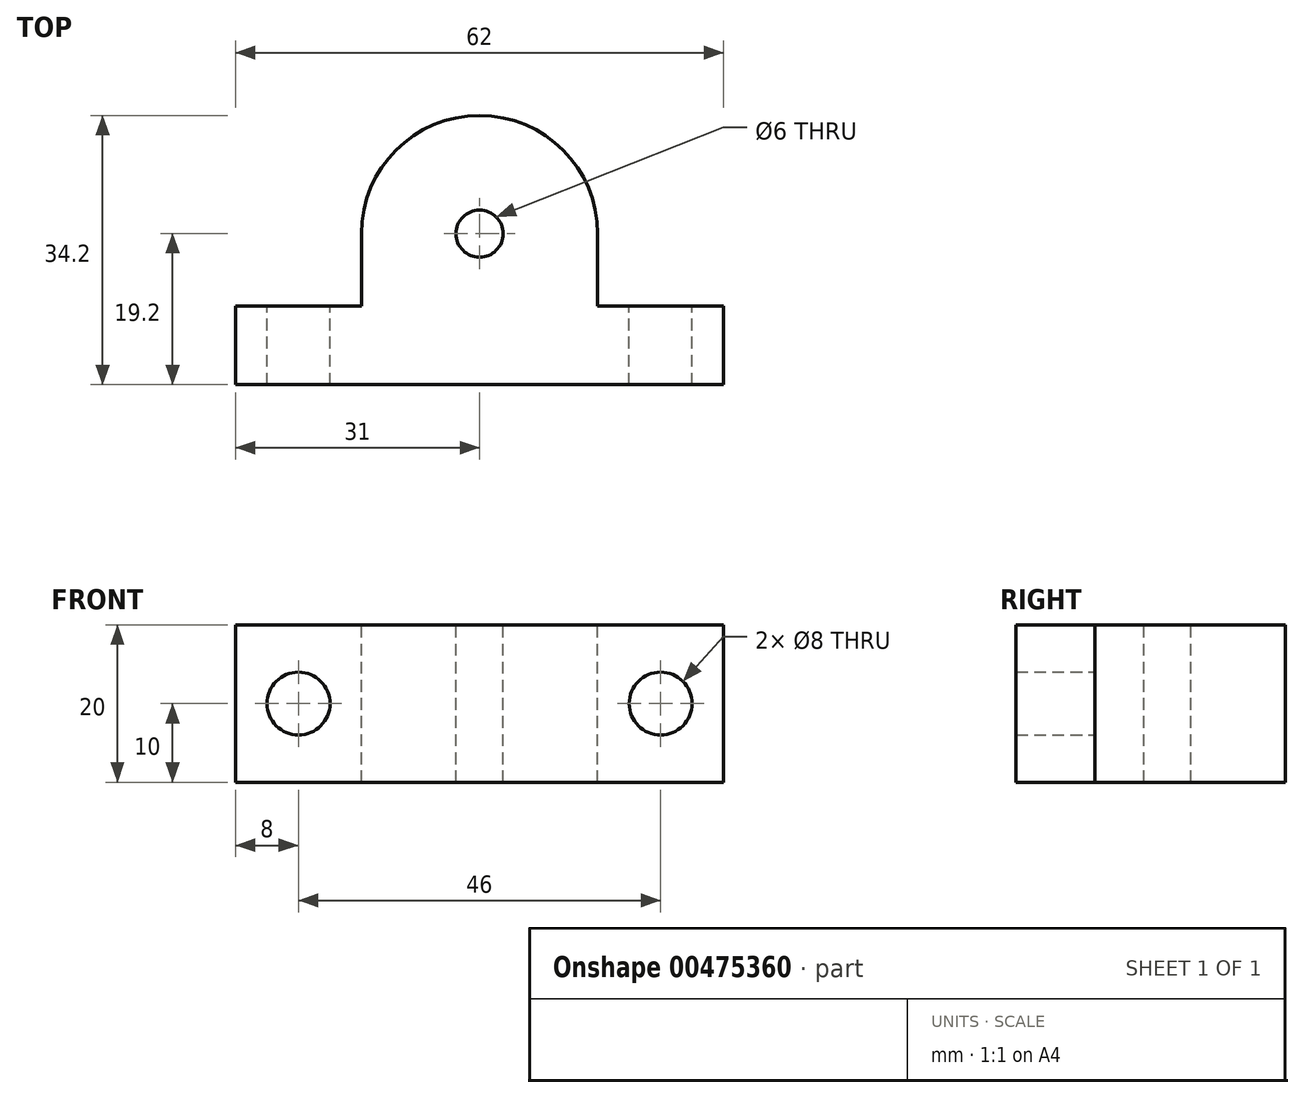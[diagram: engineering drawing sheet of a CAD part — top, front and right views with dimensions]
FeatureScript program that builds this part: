
annotation { "Feature Type Name" : "Feature", "Feature Type Description" : "" }
export const myFeature = defineFeature(function(context is Context, id is Id, definition is map)
    precondition{}
    {
        {
            var Q0;
            Q0=qCreatedBy(makeId("Top.planeOp"),FACE);
            var sketch = newSketch(context, id + "F0", { "sketchPlane" : qUnion([Q0])});
            skLineSegment(sketch, "E0.bottom", {"start": v(28, -19.2) * mm, "end": v(-28, -19.2) * mm});
            skLineSegment(sketch, "E0.top", {"start": v(28, 0) * mm, "end": v(-28, 0) * mm});
            skLineSegment(sketch, "E0.left", {"start": v(28, -19.2) * mm, "end": v(28, 0) * mm});
            skLineSegment(sketch, "E0.right", {"start": v(-28, -19.2) * mm, "end": v(-28, 0) * mm});
            skPoint(sketch, "E0.middle", {"position": v(0, -9.6) * mm});
            skCircle(sketch, "E1", {"center": v(0, 0) * mm, "radius": 9.5 * mm});
            skArc(sketch, "E2", {"start": v(-15, 0) * mm, "mid": v(0, 15) * mm, "end": v(15, 0) * mm});
            skLineSegment(sketch, "E3", {"start": v(-28, -9.2) * mm, "end": v(-11, -9.2) * mm});
            skLineSegment(sketch, "E4", {"start": v(-11, -9.2) * mm, "end": v(-11, -19.2) * mm});
            skLineSegment(sketch, "E5", {"start": v(11, -19.2) * mm, "end": v(11, -9.2) * mm});
            skLineSegment(sketch, "E6", {"start": v(11, -9.2) * mm, "end": v(28, -9.2) * mm});
            skLineSegment(sketch, "E7", {"start": v(-28, 0) * mm, "end": v(-28, 8.5) * mm});
            skLineSegment(sketch, "E8", {"start": v(-28, 8.5) * mm, "end": v(28, 8.5) * mm});
            skLineSegment(sketch, "E9", {"start": v(28, 8.5) * mm, "end": v(28, 0) * mm});
            skPoint(sketch, "E10", {"position": v(-19, 0) * mm});
            skLineSegment(sketch, "E11", {"start": v(-28, 3.17) * mm, "end": v(-28, 0) * mm});
            skPoint(sketch, "E12", {"position": v(28, 0) * mm});
            skPoint(sketch, "E13", {"position": v(19, 0) * mm});
            skPoint(sketch, "E14", {"position": v(25.5, 0) * mm});
            skPoint(sketch, "E15", {"position": v(12.4, 0) * mm});
            skPoint(sketch, "E16", {"position": v(0, 21) * mm});
            skLineSegment(sketch, "E17", {"start": v(0, 21) * mm, "end": v(-28, 13.5) * mm});
            skPoint(sketch, "E18", {"position": v(-25.5, 0) * mm});
            skLineSegment(sketch, "E19", {"start": v(-25.5, 0) * mm, "end": v(-25.5, 14.17) * mm});
            skPoint(sketch, "E20", {"position": v(-25.5, 8.67) * mm});
            skPoint(sketch, "E21", {"position": v(-12.4, 0) * mm});
            skLineSegment(sketch, "E22", {"start": v(-25.5, 8.67) * mm, "end": v(-12.24, 8.67) * mm});
            skPoint(sketch, "E23", {"position": v(-19, 8.67) * mm});
            skLineSegment(sketch, "E24", {"start": v(31, 8.5) * mm, "end": v(31, -9.2) * mm});
            skLineSegment(sketch, "E25", {"start": v(28, 8.5) * mm, "end": v(31, 8.5) * mm});
            skLineSegment(sketch, "E26", {"start": v(-28, 8.5) * mm, "end": v(-31, 8.5) * mm});
            skLineSegment(sketch, "E27", {"start": v(-31, 8.5) * mm, "end": v(-31, -9.2) * mm});
            skLineSegment(sketch, "E28", {"start": v(-31, -9.2) * mm, "end": v(-28, -9.2) * mm});
            skLineSegment(sketch, "E29", {"start": v(31, -9.2) * mm, "end": v(28, -9.2) * mm});
            skLineSegment(sketch, "E30", {"start": v(31, -9.2) * mm, "end": v(31, -19.2) * mm});
            skLineSegment(sketch, "E31", {"start": v(31, -19.2) * mm, "end": v(28, -19.2) * mm});
            skLineSegment(sketch, "E32", {"start": v(-31, -9.2) * mm, "end": v(-31, -19.2) * mm});
            skLineSegment(sketch, "E33", {"start": v(-31, -19.2) * mm, "end": v(-28, -19.2) * mm});
            skLineSegment(sketch, "E34", {"start": v(15, 0) * mm, "end": v(15, -9.2) * mm});
            skLineSegment(sketch, "E35", {"start": v(-15, 0) * mm, "end": v(-15, -9.2) * mm});
            skSolve(sketch);
        }
        {
            var Q0;
            {var subQ1=sQuery(id+"F0.wireOp",EDGE,"E0.top");var subQ3=sQuery(id+"F0.wireOp",EDGE,"E1");var subQ4=makeQuery(id+"F0.imprint","INTERSECT",VERTEX,{"disambiguationData":[OD(1.0)],"derivedFrom":[subQ1,subQ3]});Q0=makeQuery(id+"F0.imprint","IMPRINT",FACE,{"disambiguationData":[TD([[makeQuery(id+"F0.imprint","IMPRINT",EDGE,{"disambiguationData":[TD([[subQ4,1.0]])],"derivedFrom":subQ3}),-1.0]])]});}
            var Q1;
            {var subQ0=sQuery(id+"F0.wireOp",EDGE,"E8");var subQ1=sQuery(id+"F0.wireOp",EDGE,"E1");var subQ7=makeQuery(id+"F0.imprint","INTERSECT",VERTEX,{"disambiguationData":[OD(0.0)],"derivedFrom":[subQ1,subQ0]});Q1=makeQuery(id+"F0.imprint","IMPRINT",FACE,{"disambiguationData":[TD([[makeQuery(id+"F0.imprint","IMPRINT",EDGE,{"disambiguationData":[TD([[subQ7,-1.0]])],"derivedFrom":subQ1}),-1.0]])]});}
            var Q2;
            {var subQ0=sQuery(id+"F0.wireOp",EDGE,"E1");var subQ1=sQuery(id+"F0.wireOp",EDGE,"E0.top");var subQ2=makeQuery(id+"F0.imprint","INTERSECT",VERTEX,{"disambiguationData":[OD(0.0)],"derivedFrom":[subQ1,subQ0]});Q2=makeQuery(id+"F0.imprint","IMPRINT",FACE,{"disambiguationData":[TD([[makeQuery(id+"F0.imprint","IMPRINT",EDGE,{"disambiguationData":[TD([[subQ2,-1.0]])],"derivedFrom":subQ1}),-1.0]])]});}
            var Q3;
            {var subQ0=sQuery(id+"F0.wireOp",EDGE,"E8");var subQ1=sQuery(id+"F0.wireOp",EDGE,"E1");var subQ2=makeQuery(id+"F0.imprint","INTERSECT",VERTEX,{"disambiguationData":[OD(0.0)],"derivedFrom":[subQ1,subQ0]});Q3=makeQuery(id+"F0.imprint","IMPRINT",FACE,{"disambiguationData":[TD([[makeQuery(id+"F0.imprint","IMPRINT",EDGE,{"disambiguationData":[TD([[subQ2,-1.0]])],"derivedFrom":subQ1}),1.0]])]});}
            var Q4;
            {var subQ1=sQuery(id+"F0.wireOp",EDGE,"E0.top");var subQ3=sQuery(id+"F0.wireOp",EDGE,"E1");var subQ4=makeQuery(id+"F0.imprint","INTERSECT",VERTEX,{"disambiguationData":[OD(0.0)],"derivedFrom":[subQ1,subQ3]});Q4=makeQuery(id+"F0.imprint","IMPRINT",FACE,{"disambiguationData":[TD([[makeQuery(id+"F0.imprint","IMPRINT",EDGE,{"disambiguationData":[TD([[subQ4,-1.0]])],"derivedFrom":subQ3}),-1.0]])]});}
            var Q5;
            {var subQ0=sQuery(id+"F0.wireOp",EDGE,"E1");var subQ1=sQuery(id+"F0.wireOp",EDGE,"E0.top");var subQ2=makeQuery(id+"F0.imprint","INTERSECT",VERTEX,{"disambiguationData":[OD(0.0)],"derivedFrom":[subQ1,subQ0]});Q5=makeQuery(id+"F0.imprint","IMPRINT",FACE,{"disambiguationData":[TD([[makeQuery(id+"F0.imprint","IMPRINT",EDGE,{"disambiguationData":[TD([[subQ2,-1.0]])],"derivedFrom":subQ1}),1.0]])]});}
            var Q6;
            {var subQ7=sQuery(id+"F0.wireOp",EDGE,"E4");Q6=makeQuery(id+"F0.imprint","IMPRINT",FACE,{"disambiguationData":[TD([[makeQuery(id+"F0.imprint","IMPRINT",EDGE,{"derivedFrom":subQ7}),1.0]])]});}
            var Q7;
            {var subQ6=sQuery(id+"F0.wireOp",EDGE,"E4");Q7=makeQuery(id+"F0.imprint","IMPRINT",FACE,{"disambiguationData":[TD([[makeQuery(id+"F0.imprint","IMPRINT",EDGE,{"derivedFrom":subQ6}),-1.0]])]});}
            var Q8;
            {var subQ2=sQuery(id+"F0.wireOp",EDGE,"E28");Q8=makeQuery(id+"F0.imprint","IMPRINT",FACE,{"disambiguationData":[TD([[makeQuery(id+"F0.imprint","IMPRINT",EDGE,{"derivedFrom":subQ2}),-1.0]])]});}
            var Q9;
            {var subQ0=sQuery(id+"F0.wireOp",EDGE,"E5");Q9=makeQuery(id+"F0.imprint","IMPRINT",FACE,{"disambiguationData":[TD([[makeQuery(id+"F0.imprint","IMPRINT",EDGE,{"derivedFrom":subQ0}),-1.0]])]});}
            var Q10;
            {var subQ2=sQuery(id+"F0.wireOp",EDGE,"E29");Q10=makeQuery(id+"F0.imprint","IMPRINT",FACE,{"disambiguationData":[TD([[makeQuery(id+"F0.imprint","IMPRINT",EDGE,{"derivedFrom":subQ2}),1.0]])]});}
            extrude(context, id + "F1", {"entities" : qUnion([Q0, Q1, Q2, Q3, Q4, Q5, Q6, Q7, Q8, Q9, Q10]), "oppositeDirection" : true, "depth" : 20 * mm});
        }
        {
            var Q0;
            Q0=sQuery(id+"F0.wireOp",VERTEX,"E2.center");
            var Q1;
            Q1=makeQuery(id+"F1.opExtrude","SWEPT_BODY",BODY,{"disambiguationData":[OSD([sQuery(id+"F0.wireOp",EDGE,"E0.bottom"),sQuery(id+"F0.wireOp",EDGE,"E0.left"),sQuery(id+"F0.wireOp",EDGE,"E0.right"),sQuery(id+"F0.wireOp",EDGE,"E2"),sQuery(id+"F0.wireOp",EDGE,"E3"),sQuery(id+"F0.wireOp",EDGE,"E4"),sQuery(id+"F0.wireOp",EDGE,"E5"),sQuery(id+"F0.wireOp",EDGE,"E6"),sQuery(id+"F0.wireOp",EDGE,"E7"),sQuery(id+"F0.wireOp",EDGE,"E8"),sQuery(id+"F0.wireOp",EDGE,"E9"),sQuery(id+"F0.wireOp",EDGE,"E11")])]});
            hole(context, id + "F2", {"style" : HoleStyle.SIMPLE, "endStyle" : HoleEndStyle.THROUGH, "standardTappedOrClearance" : lookupTablePath({ "standard" : "ISO", "size" : "6", "type" : "Drilled" }), "standardBlindInLast" : lookupTablePath({ "standard" : "ISO", "size" : "6", "type" : "Drilled" }), "holeDiameter" : 6 * mm, "isTappedThrough" : true, "tappedDepth" : 12 * mm, "tapClearance" : 3, "locations" : qUnion([Q0]), "scope" : qUnion([Q1])});
        }
        {
            var Q0;
            Q0=makeQuery(id+"F1.opExtrude","SWEPT_FACE",FACE,{"disambiguationData":[OSD([sQuery(id+"F0.wireOp",EDGE,"E6"),sQuery(id+"F0.wireOp",EDGE,"E29")])]});
            var sketch = newSketch(context, id + "F3", { "sketchPlane" : qUnion([Q0])});
            skPoint(sketch, "E36", {"position": v(-23, -10) * mm});
            skPoint(sketch, "E36.positionSnap0", {"position": v(-23, 0) * mm});
            skPoint(sketch, "E36.positionSnap1", {"position": v(-31, -10) * mm});
            skSolve(sketch);
        }
        {
            var Q0;
            Q0=makeQuery(id+"F1.opExtrude","SWEPT_FACE",FACE,{"disambiguationData":[OSD([sQuery(id+"F0.wireOp",EDGE,"E3"),sQuery(id+"F0.wireOp",EDGE,"E28")])]});
            var sketch = newSketch(context, id + "F4", { "sketchPlane" : qUnion([Q0])});
            skPoint(sketch, "E37", {"position": v(23, -10) * mm});
            skPoint(sketch, "E37.positionSnap0", {"position": v(31, -10) * mm});
            skPoint(sketch, "E37.positionSnap1", {"position": v(23, 0) * mm});
            skSolve(sketch);
        }
        {
            var Q0;
            Q0=sQuery(id+"F3.wireOp",VERTEX,"E36");
            var Q1;
            Q1=sQuery(id+"F4.wireOp",VERTEX,"E37");
            var Q2;
            Q2=makeQuery(id+"F1.opExtrude","SWEPT_BODY",BODY,{"disambiguationData":[OSD([sQuery(id+"F0.wireOp",EDGE,"E0.bottom"),sQuery(id+"F0.wireOp",EDGE,"E2"),sQuery(id+"F0.wireOp",EDGE,"E3"),sQuery(id+"F0.wireOp",EDGE,"E6"),sQuery(id+"F0.wireOp",EDGE,"E28"),sQuery(id+"F0.wireOp",EDGE,"E29"),sQuery(id+"F0.wireOp",EDGE,"E30"),sQuery(id+"F0.wireOp",EDGE,"E31"),sQuery(id+"F0.wireOp",EDGE,"E32"),sQuery(id+"F0.wireOp",EDGE,"E33"),sQuery(id+"F0.wireOp",EDGE,"E34"),sQuery(id+"F0.wireOp",EDGE,"E35")])]});
            hole(context, id + "F5", {"style" : HoleStyle.SIMPLE, "endStyle" : HoleEndStyle.THROUGH, "standardTappedOrClearance" : lookupTablePath({ "standard" : "ISO", "size" : "8", "type" : "Drilled" }), "standardBlindInLast" : lookupTablePath({ "standard" : "ISO", "size" : "8", "type" : "Drilled" }), "holeDiameter" : 8 * mm, "isTappedThrough" : true, "tappedDepth" : 12 * mm, "tapClearance" : 3, "locations" : qUnion([Q0, Q1]), "scope" : qUnion([Q2])});
        }
    });
